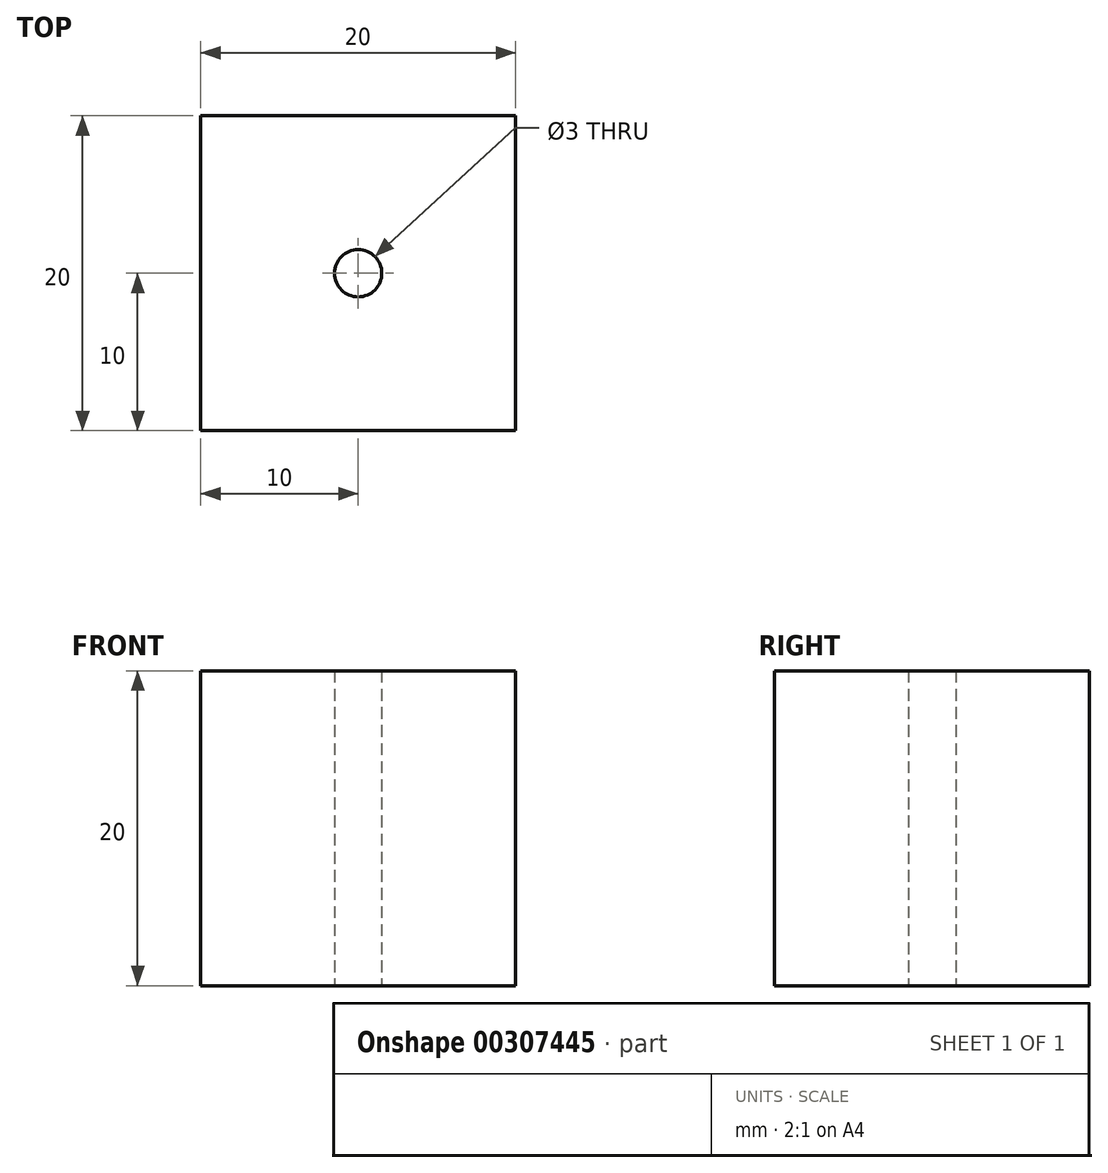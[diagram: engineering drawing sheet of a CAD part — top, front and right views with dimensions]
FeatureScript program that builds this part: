
annotation { "Feature Type Name" : "Feature", "Feature Type Description" : "" }
export const myFeature = defineFeature(function(context is Context, id is Id, definition is map)
    precondition{}
    {
        {
            var Q0;
            Q0=qCreatedBy(makeId("Top.planeOp"),FACE);
            var sketch = newSketch(context, id + "F0", { "sketchPlane" : qUnion([Q0])});
            skLineSegment(sketch, "E0.bottom", {"start": v(0, 0) * mm, "end": v(20, 0) * mm});
            skLineSegment(sketch, "E0.top", {"start": v(0, 20) * mm, "end": v(20, 20) * mm});
            skLineSegment(sketch, "E0.left", {"start": v(0, 0) * mm, "end": v(0, 20) * mm});
            skLineSegment(sketch, "E0.right", {"start": v(20, 0) * mm, "end": v(20, 20) * mm});
            skLineSegment(sketch, "E1", {"start": v(0, 10) * mm, "end": v(20, 10) * mm, "construction": true});
            skLineSegment(sketch, "E2", {"start": v(10, 20) * mm, "end": v(10, 0) * mm, "construction": true});
            skCircle(sketch, "E3", {"center": v(10, 10) * mm, "radius": 1.5 * mm});
            skSolve(sketch);
        }
        {
            var Q0;
            Q0=makeQuery(id+"F0.imprint","IMPRINT",FACE,{"disambiguationData":[TD([[makeQuery(id+"F0.imprint","IMPRINT",EDGE,{"derivedFrom":sQuery(id+"F0.wireOp",EDGE,"E0.bottom")}),1.0]])]});
            extrude(context, id + "F1", {"entities" : qUnion([Q0]), "depth" : 20 * mm});
        }
    });
